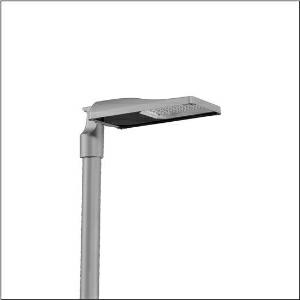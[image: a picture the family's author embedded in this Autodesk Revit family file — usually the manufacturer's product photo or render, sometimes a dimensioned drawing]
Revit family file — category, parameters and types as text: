
# Revit family: streetlight_sl_31_mini___st1_0a_5xh2d71b08ha_8b0a
name_source: partatom
category: Lighting Fixtures
units: mm (PartAtom-declared; Revit-internal decimal feet)

## family parameters
Cut with Voids When Loaded = No
Host = Face
Light Source = No
Part Type = Normal
Room Calculation Point = No
Round Connector Dimension = Use Diameter
Shared = No

## types (1)
- --- (1 x LED, 7470 lm, 68.3 W, 2200K)
    Apparent Load = 68 VA
    CIE Flux Codes = 37 72 97 100 100
    Color Rendering = 70
    Color Temperature = 2200K
    Default Elevation = 1800 mm
    Description = Streetlight SL 31 mini Easy, LST, Desk-Remote mast luminaire for post-top, side-entry; light control with lens of PMMA; light distribution: ST1.0a, direct asymmetric distribution, for standard-compliant lighting for roads and squares; LED: luminous flux: 7.470lm, light colour: 722, colour temperature: 2200K; luminous efficacy: 109,4lm/W; control: pre-setting: linear dimming characteristic, flexible luminous flux parameterisation, time-dependent luminous flux control, constant luminous flux control, power reduction, intelligent temperature release in ECG and LED module, overheat protection; luminaire housing, of diecast aluminium, Siteco® metallic grey (DB 702S), corrosivity category C5 high according to DIN EN ISO 12944; cover of toughened safety glass, transparent, mast flange of diecast aluminium, Siteco® metallic grey (DB 702S), spigot size: 76/60mm, mast flange included unmounted; with cable H07RN-F 3x 1.5mm², cable length: 8,5m, connection cable pre-assembled; mains connection: 220..240V, AC, 50/60Hz; power consumption (at start of service life): 68,3W / (at end of service life): 74,8W / (with reduced operation 50%): 29,4W; protection rating (complete): IP66; insulation class (complete): insulation class II (safety insulation); impact resistance: IK10; certification: CE, ENEC, ENEC+, VDE, UKCA; permissible operating ambient temperature for outdoor applications: -40..+50°C; packaging unit: 1 piece

Light Distribution: ST1.0a
    Height = 76 mm
    Lamp = 1 x LED
    Lamp Light Flux = 7470 lm
    Lamp Power = 68.3 W
    Lamp count = 1
    Length = 547 mm
    Luminous efficacy = 109 lm/W
    Manufacturer = Siteco
    ModVariant = No
    Model = 5XH2D71B08HA
    Number of Poles = 1
    OnlyDefault = Yes
    Power Factor = 1
    Product Name = Streetlight SL 31 mini | ST1.0a
    Product group = mast luminaire | pylon top
    ProductGroupID = 6100
    Protection Class = Protection class II
    Protection Degree = IP 66
    RLX_Detail_Level = 1
    RLX_Emergency_Light_Flux = 0 lm
    RLX_Emergency_Type = 0
    RLX_Emergency_Type_DB = No
    RlxData = <blob elided: 39389 chars, md5=645433dc>
    Socket = socket
    Standby Power = 0 W
    System Light Flux = 7470 lm
    System Power = 68 W
    Type Comments = factory setting: luminous flux: 100 % | dim-lin: 254 | 693 mA
    Type Image = l_1300326.jpg
    URL = http://relux.com
    VarID = @adj_008783
    Voltage = 0 V
    Weight = 0.00 kg
    Width = 265 mm

## geometry (parser evidence)
native form markers: Blend x4, Sweep x9
no freeform markers — native parametric forms only
